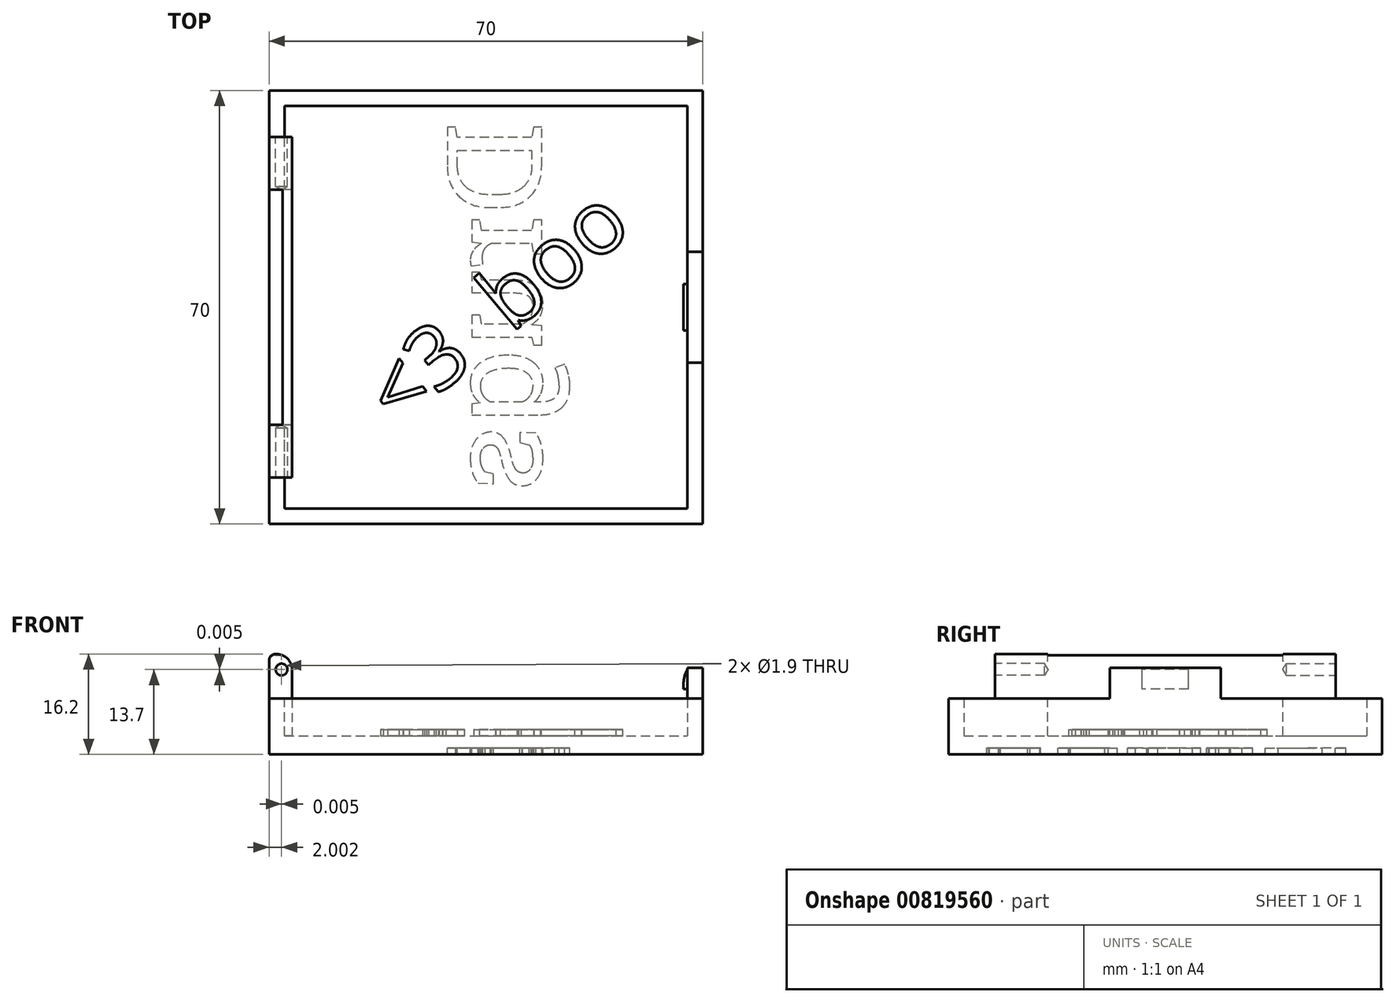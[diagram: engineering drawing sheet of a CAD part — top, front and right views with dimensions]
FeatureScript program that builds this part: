
annotation { "Feature Type Name" : "Feature", "Feature Type Description" : "" }
export const myFeature = defineFeature(function(context is Context, id is Id, definition is map)
    precondition{}
    {
        {
            var Q0;
            Q0=qCreatedBy(makeId("Top.planeOp"),FACE);
            var sketch = newSketch(context, id + "F0", { "sketchPlane" : qUnion([Q0])});
            skLineSegment(sketch, "E0.bottom", {"start": v(-37.36, -39.62) * mm, "end": v(27.64, -39.62) * mm});
            skLineSegment(sketch, "E0.top", {"start": v(-37.36, 25.38) * mm, "end": v(27.64, 25.38) * mm});
            skLineSegment(sketch, "E0.left", {"start": v(-37.36, -39.62) * mm, "end": v(-37.36, 25.38) * mm});
            skLineSegment(sketch, "E0.right", {"start": v(27.64, -39.62) * mm, "end": v(27.64, 25.38) * mm});
            skLineSegment(sketch, "E1.bottom", {"start": v(-39.86, 27.88) * mm, "end": v(30.14, 27.88) * mm});
            skLineSegment(sketch, "E1.top", {"start": v(-39.86, -42.12) * mm, "end": v(30.14, -42.12) * mm});
            skLineSegment(sketch, "E1.left", {"start": v(-39.86, 27.88) * mm, "end": v(-39.86, -42.12) * mm});
            skLineSegment(sketch, "E1.right", {"start": v(30.14, 27.88) * mm, "end": v(30.14, -42.12) * mm});
            skSolve(sketch);
        }
        {
            var Q0;
            Q0=makeQuery(id+"F0.imprint","IMPRINT",FACE,{"disambiguationData":[TD([[makeQuery(id+"F0.imprint","IMPRINT",EDGE,{"derivedFrom":sQuery(id+"F0.wireOp",EDGE,"E0.bottom")}),-1.0]])]});
            extrude(context, id + "F1", {"entities" : qUnion([Q0]), "depth" : 8 * mm, "offsetDistance" : 25 * mm});
        }
        {
            var Q0;
            Q0=makeQuery(id+"F0.imprint","IMPRINT",FACE,{"disambiguationData":[TD([[makeQuery(id+"F0.imprint","IMPRINT",EDGE,{"derivedFrom":sQuery(id+"F0.wireOp",EDGE,"E0.bottom")}),1.0]])]});
            extrude(context, id + "F2", {"entities" : qUnion([Q0]), "operationType" : NewBodyOperationType.ADD, "depth" : 2 * mm, "offsetDistance" : 25 * mm});
        }
        {
            var Q0;
            Q0=makeQuery(id+"F1.opExtrude","CAP_FACE",FACE,{"disambiguationData":[OSD([sQuery(id+"F0.wireOp",EDGE,"E0.bottom"),sQuery(id+"F0.wireOp",EDGE,"E0.top"),sQuery(id+"F0.wireOp",EDGE,"E0.left"),sQuery(id+"F0.wireOp",EDGE,"E0.right"),sQuery(id+"F0.wireOp",EDGE,"E1.bottom"),sQuery(id+"F0.wireOp",EDGE,"E1.top"),sQuery(id+"F0.wireOp",EDGE,"E1.left"),sQuery(id+"F0.wireOp",EDGE,"E1.right")])],"isStart":false});
            var sketch = newSketch(context, id + "F3", { "sketchPlane" : qUnion([Q0])});
            skLineSegment(sketch, "E2.bottom", {"start": v(30.14, -16.06) * mm, "end": v(27.64, -16.06) * mm});
            skLineSegment(sketch, "E2.top", {"start": v(30.14, 1.82) * mm, "end": v(27.64, 1.82) * mm});
            skLineSegment(sketch, "E2.left", {"start": v(30.14, -16.06) * mm, "end": v(30.14, 1.82) * mm});
            skLineSegment(sketch, "E2.right", {"start": v(27.64, -16.06) * mm, "end": v(27.64, 1.82) * mm});
            skPoint(sketch, "E3", {"position": v(30.14, -7.12) * mm});
            skSolve(sketch);
        }
        {
            var Q0;
            Q0=makeQuery(id+"F3.imprint","IMPRINT",FACE,{"disambiguationData":[TD([[makeQuery(id+"F3.imprint","IMPRINT",EDGE,{"derivedFrom":sQuery(id+"F3.wireOp",EDGE,"E2.bottom")}),-1.0]])]});
            extrude(context, id + "F4", {"entities" : qUnion([Q0]), "operationType" : NewBodyOperationType.ADD, "depth" : 5 * mm, "offsetDistance" : 25 * mm});
        }
        {
            var Q0;
            Q0=makeQuery(id+"F4.boolean.opBoolean","MERGE",FACE,{"derivedFrom":[makeQuery(id+"F1.opExtrude","SWEPT_FACE",FACE,{"disambiguationData":[OSD([sQuery(id+"F0.wireOp",EDGE,"E0.right")])]}),makeQuery(id+"F4.opExtrude","SWEPT_FACE",FACE,{"disambiguationData":[OSD([sQuery(id+"F3.wireOp",EDGE,"E2.right")])]})]});
            var sketch = newSketch(context, id + "F5", { "sketchPlane" : qUnion([Q0])});
            skLineSegment(sketch, "E4.bottom", {"start": v(3.38, 9.55) * mm, "end": v(10.86, 9.55) * mm});
            skLineSegment(sketch, "E4.top", {"start": v(3.38, 12.75) * mm, "end": v(10.86, 12.75) * mm});
            skLineSegment(sketch, "E4.left", {"start": v(3.38, 9.55) * mm, "end": v(3.38, 12.75) * mm});
            skLineSegment(sketch, "E4.right", {"start": v(10.86, 9.55) * mm, "end": v(10.86, 12.75) * mm});
            skSolve(sketch);
        }
        {
            var Q0;
            Q0=makeQuery(id+"F5.imprint","IMPRINT",FACE,{"disambiguationData":[TD([[makeQuery(id+"F5.imprint","IMPRINT",EDGE,{"derivedFrom":sQuery(id+"F5.wireOp",EDGE,"E4.bottom")}),1.0]])]});
            extrude(context, id + "F6", {"entities" : qUnion([Q0]), "operationType" : NewBodyOperationType.ADD, "depth" : .6 * mm, "offsetDistance" : 25 * mm});
        }
        {
            var Q0;
            Q0=makeQuery(id+"F6.opExtrude","CAP_EDGE",EDGE,{"disambiguationData":[OSD([sQuery(id+"F5.wireOp",EDGE,"E4.top")])],"isStart":false});
            fillet(context, id + "F7", {"entities" : qUnion([Q0]), "radius" : 5 * mm, "tangentPropagation" : true, "allowEdgeOverflow" : false});
        }
        {
            var Q0;
            Q0=makeQuery(id+"F1.opExtrude","CAP_FACE",FACE,{"disambiguationData":[OSD([sQuery(id+"F0.wireOp",EDGE,"E0.bottom"),sQuery(id+"F0.wireOp",EDGE,"E0.top"),sQuery(id+"F0.wireOp",EDGE,"E0.left"),sQuery(id+"F0.wireOp",EDGE,"E0.right"),sQuery(id+"F0.wireOp",EDGE,"E1.bottom"),sQuery(id+"F0.wireOp",EDGE,"E1.top"),sQuery(id+"F0.wireOp",EDGE,"E1.left"),sQuery(id+"F0.wireOp",EDGE,"E1.right")])],"isStart":false});
            var sketch = newSketch(context, id + "F8", { "sketchPlane" : qUnion([Q0])});
            skLineSegment(sketch, "E5.bottom", {"start": v(-39.86, 11.88) * mm, "end": v(-36.16, 11.88) * mm});
            skLineSegment(sketch, "E5.top", {"start": v(-39.86, -26.12) * mm, "end": v(-36.16, -26.12) * mm});
            skLineSegment(sketch, "E5.left", {"start": v(-39.86, 11.88) * mm, "end": v(-39.86, -26.12) * mm});
            skLineSegment(sketch, "E5.right", {"start": v(-36.16, 11.88) * mm, "end": v(-36.16, -26.12) * mm});
            skSolve(sketch);
        }
        {
            var Q0;
            {var subQ0=sQuery(id+"F8.wireOp",EDGE,"E5.right");Q0=makeQuery(id+"F8.imprint","IMPRINT",FACE,{"disambiguationData":[TD([[makeQuery(id+"F8.imprint","IMPRINT",EDGE,{"derivedFrom":subQ0}),-1.0]])]});}
            var Q1;
            {var subQ0=sQuery(id+"F8.wireOp",EDGE,"E5.left");Q1=makeQuery(id+"F8.imprint","IMPRINT",FACE,{"disambiguationData":[TD([[makeQuery(id+"F8.imprint","IMPRINT",EDGE,{"derivedFrom":subQ0}),1.0]])]});}
            extrude(context, id + "F9", {"entities" : qUnion([Q0, Q1]), "operationType" : NewBodyOperationType.ADD, "depth" : 7 * mm, "offsetDistance" : 25 * mm});
        }
        {
            var Q0;
            {var subQ0=sQuery(id+"F8.wireOp",EDGE,"E5.right");Q0=makeQuery(id+"F8.imprint","IMPRINT",FACE,{"disambiguationData":[TD([[makeQuery(id+"F8.imprint","IMPRINT",EDGE,{"derivedFrom":subQ0}),-1.0]])]});}
            extrude(context, id + "F10", {"entities" : qUnion([Q0]), "operationType" : NewBodyOperationType.ADD, "endBound" : BoundingType.UP_TO_NEXT, "oppositeDirection" : true, "depth" : 5 * mm, "offsetDistance" : 25 * mm});
        }
        {
            var Q0;
            {var subQ0=sQuery(id+"F0.wireOp",EDGE,"E0.top");var subQ1=sQuery(id+"F0.wireOp",EDGE,"E1.right");var subQ2=sQuery(id+"F0.wireOp",EDGE,"E1.left");var subQ3=sQuery(id+"F0.wireOp",EDGE,"E0.left");var subQ5=sQuery(id+"F0.wireOp",EDGE,"E0.right");var subQ6=sQuery(id+"F0.wireOp",EDGE,"E1.bottom");Q0=makeQuery(id+"F9.boolean.opBoolean","SPLIT",FACE,{"disambiguationData":[TD([makeQuery(id+"F1.opExtrude","SWEPT_FACE",FACE,{"disambiguationData":[OSD([subQ0])]})])],"derivedFrom":makeQuery(id+"F1.opExtrude","CAP_FACE",FACE,{"disambiguationData":[OSD([sQuery(id+"F0.wireOp",EDGE,"E0.bottom"),subQ0,subQ3,subQ5,subQ6,sQuery(id+"F0.wireOp",EDGE,"E1.top"),subQ2,subQ1])],"isStart":false})});}
            var sketch = newSketch(context, id + "F11", { "sketchPlane" : qUnion([Q0])});
            skLineSegment(sketch, "E6.bottom", {"start": v(-39.86, 20.38) * mm, "end": v(-36.16, 20.38) * mm});
            skLineSegment(sketch, "E6.top", {"start": v(-39.86, 11.88) * mm, "end": v(-36.16, 11.88) * mm});
            skLineSegment(sketch, "E6.left", {"start": v(-39.86, 20.38) * mm, "end": v(-39.86, 11.88) * mm});
            skLineSegment(sketch, "E6.right", {"start": v(-36.16, 20.38) * mm, "end": v(-36.16, 11.88) * mm});
            skLineSegment(sketch, "E7.bottom", {"start": v(-39.85, -26.11) * mm, "end": v(-36.15, -26.11) * mm});
            skLineSegment(sketch, "E7.top", {"start": v(-39.85, -34.61) * mm, "end": v(-36.15, -34.61) * mm});
            skLineSegment(sketch, "E7.left", {"start": v(-39.85, -26.11) * mm, "end": v(-39.85, -34.61) * mm});
            skLineSegment(sketch, "E7.right", {"start": v(-36.15, -26.11) * mm, "end": v(-36.15, -34.61) * mm});
            skSolve(sketch);
        }
        {
            var Q0;
            Q0=qSketchRegion(id+"F11",true);
            extrude(context, id + "F12", {"entities" : qUnion([Q0]), "operationType" : NewBodyOperationType.ADD, "depth" : 7.2 * mm, "offsetDistance" : 25 * mm});
        }
        {
            var Q0;
            Q0=makeQuery(id+"F12.opExtrude","SWEPT_FACE",FACE,{"disambiguationData":[OSD([sQuery(id+"F11.wireOp",EDGE,"E6.bottom")])]});
            var sketch = newSketch(context, id + "F13", { "sketchPlane" : qUnion([Q0])});
            skPoint(sketch, "E8", {"position": v(37.86, 12.7) * mm});
            skPoint(sketch, "E9", {"position": v(14.71, -29.21) * mm});
            skPoint(sketch, "E10", {"position": v(38, 15.2) * mm});
            skSolve(sketch);
        }
        {
            var Q0;
            Q0=sQuery(id+"F13.wireOp",VERTEX,"E8");
            var Q1;
            Q1=makeQuery(id+"F1.opExtrude","SWEPT_BODY",BODY,{"disambiguationData":[OSD([sQuery(id+"F0.wireOp",EDGE,"E0.bottom"),sQuery(id+"F0.wireOp",EDGE,"E0.top"),sQuery(id+"F0.wireOp",EDGE,"E0.left"),sQuery(id+"F0.wireOp",EDGE,"E0.right"),sQuery(id+"F0.wireOp",EDGE,"E1.bottom"),sQuery(id+"F0.wireOp",EDGE,"E1.top"),sQuery(id+"F0.wireOp",EDGE,"E1.left"),sQuery(id+"F0.wireOp",EDGE,"E1.right")])]});
            hole(context, id + "F14", {"style" : HoleStyle.SIMPLE, "endStyle" : HoleEndStyle.BLIND, "holeDiameter" : 1.9 * mm, "majorDiameter" : 5 * mm, "holeDepth" : 8 * mm, "isTappedThrough" : true, "tappedDepth" : 12 * mm, "tapClearance" : 3, "locations" : qUnion([Q0]), "scope" : qUnion([Q1])});
        }
        {
            var Q0;
            Q0=makeQuery(id+"F12.opExtrude","SWEPT_FACE",FACE,{"disambiguationData":[OSD([sQuery(id+"F11.wireOp",EDGE,"E7.top")])]});
            var sketch = newSketch(context, id + "F15", { "sketchPlane" : qUnion([Q0])});
            skPoint(sketch, "E11", {"position": v(-37.85, 12.7) * mm});
            skPoint(sketch, "E12", {"position": v(-38, 15.2) * mm});
            skSolve(sketch);
        }
        {
            var Q0;
            Q0=sQuery(id+"F15.wireOp",VERTEX,"E11");
            var Q1;
            Q1=makeQuery(id+"F1.opExtrude","SWEPT_BODY",BODY,{"disambiguationData":[OSD([sQuery(id+"F0.wireOp",EDGE,"E0.bottom"),sQuery(id+"F0.wireOp",EDGE,"E0.top"),sQuery(id+"F0.wireOp",EDGE,"E0.left"),sQuery(id+"F0.wireOp",EDGE,"E0.right"),sQuery(id+"F0.wireOp",EDGE,"E1.bottom"),sQuery(id+"F0.wireOp",EDGE,"E1.top"),sQuery(id+"F0.wireOp",EDGE,"E1.left"),sQuery(id+"F0.wireOp",EDGE,"E1.right")])]});
            hole(context, id + "F16", {"style" : HoleStyle.SIMPLE, "endStyle" : HoleEndStyle.BLIND, "holeDiameter" : 1.9 * mm, "majorDiameter" : 5 * mm, "holeDepth" : 8 * mm, "isTappedThrough" : true, "tappedDepth" : 12 * mm, "tapClearance" : 3, "locations" : qUnion([Q0]), "scope" : qUnion([Q1])});
        }
        {
            var Q0;
            {var subQ0=sQuery(id+"F0.wireOp",EDGE,"E0.right");var subQ1=sQuery(id+"F0.wireOp",EDGE,"E0.left");var subQ2=sQuery(id+"F0.wireOp",EDGE,"E0.top");var subQ3=sQuery(id+"F0.wireOp",EDGE,"E0.bottom");Q0=makeQuery(id+"F2.boolean.opBoolean","MERGE",FACE,{"derivedFrom":[makeQuery(id+"F1.opExtrude","CAP_FACE",FACE,{"disambiguationData":[OSD([subQ3,subQ2,subQ1,subQ0,sQuery(id+"F0.wireOp",EDGE,"E1.bottom"),sQuery(id+"F0.wireOp",EDGE,"E1.top"),sQuery(id+"F0.wireOp",EDGE,"E1.left"),sQuery(id+"F0.wireOp",EDGE,"E1.right")])],"isStart":true}),makeQuery(id+"F2.opExtrude","CAP_FACE",FACE,{"disambiguationData":[OSD([subQ3,subQ2,subQ1,subQ0])],"isStart":true})]});}
            var sketch = newSketch(context, id + "F17", { "sketchPlane" : qUnion([Q0])});
            skText(sketch, "E13", { "text": "Drugs", "fontName": "RobotoSlab-Regular.ttf"});
            const initialGuessF17  = {"E13": [0.00413, -0.02273, 0, 1, 0.0154]};
            skSetInitialGuess(sketch, initialGuessF17);
            skSolve(sketch);
        }
        {
            var Q0;
            Q0=makeQuery(id+"F17.imprint","IMPRINT",FACE,{"disambiguationData":[TD([[makeQuery(id+"F17.imprint","IMPRINT",EDGE,{"derivedFrom":sQuery(id+"F17.wireOp",EDGE,"E13.sketch_text.stroke-0")}),1.0]])]});
            var Q1;
            Q1=makeQuery(id+"F17.imprint","IMPRINT",FACE,{"disambiguationData":[TD([[makeQuery(id+"F17.imprint","IMPRINT",EDGE,{"derivedFrom":sQuery(id+"F17.wireOp",EDGE,"E13.sketch_text.stroke-86")}),1.0]])]});
            var Q2;
            Q2=makeQuery(id+"F17.imprint","IMPRINT",FACE,{"disambiguationData":[TD([[makeQuery(id+"F17.imprint","IMPRINT",EDGE,{"derivedFrom":sQuery(id+"F17.wireOp",EDGE,"E13.sketch_text.stroke-13")}),1.0]])]});
            var Q3;
            {var subQ0=sQuery(id+"F0.wireOp",EDGE,"E0.top");var subQ1=sQuery(id+"F0.wireOp",EDGE,"E1.right");var subQ2=sQuery(id+"F0.wireOp",EDGE,"E1.left");var subQ3=sQuery(id+"F0.wireOp",EDGE,"E0.left");var subQ5=sQuery(id+"F0.wireOp",EDGE,"E0.right");var subQ6=sQuery(id+"F0.wireOp",EDGE,"E1.bottom");Q3=makeQuery(id+"F9.boolean.opBoolean","SPLIT",FACE,{"disambiguationData":[TD([makeQuery(id+"F1.opExtrude","SWEPT_FACE",FACE,{"disambiguationData":[OSD([subQ0])]})])],"derivedFrom":makeQuery(id+"F1.opExtrude","CAP_FACE",FACE,{"disambiguationData":[OSD([sQuery(id+"F0.wireOp",EDGE,"E0.bottom"),subQ0,subQ3,subQ5,subQ6,sQuery(id+"F0.wireOp",EDGE,"E1.top"),subQ2,subQ1])],"isStart":false})});}
            var Q4;
            Q4=qConstructionFilter(qBodyType(qCreatedBy(id+"F17",EDGE),BodyType.WIRE),ConstructionObject.NO);
            extrude(context, id + "F18", {"entities" : qUnion([Q0, Q1, Q2, Q3]), "operationType" : NewBodyOperationType.ADD, "surfaceOperationType" : NewSurfaceOperationType.ADD, "surfaceEntities" : qUnion([Q4]), "depth" : 1 * mm, "offsetDistance" : 25 * mm});
        }
        {
            var Q0;
            Q0=makeQuery(id+"F2.opExtrude","CAP_FACE",FACE,{"disambiguationData":[OSD([sQuery(id+"F0.wireOp",EDGE,"E0.bottom"),sQuery(id+"F0.wireOp",EDGE,"E0.top"),sQuery(id+"F0.wireOp",EDGE,"E0.left"),sQuery(id+"F0.wireOp",EDGE,"E0.right")])],"isStart":false});
            var sketch = newSketch(context, id + "F19", { "sketchPlane" : qUnion([Q0])});
            skText(sketch, "E14", { "text": "<3  boo", "fontName": "OpenSans-Regular.ttf"});
            skLineSegment(sketch, "E15.0", {"start": v(-19.03, -26.77) * mm, "end": v(19.28, 5.37) * mm, "construction": true});
            skLineSegment(sketch, "E15.1", {"start": v(-19.03, -26.77) * mm, "end": v(-19.03, -26.77) * mm});
            const initialGuessF19  = {"E14": [-0.01903, -0.02677, 0.76604, 0.64279, 0.0103]};
            skSetInitialGuess(sketch, initialGuessF19);
            skSolve(sketch);
        }
        {
            var Q0;
            Q0=qSketchRegion(id+"F19",true);
            extrude(context, id + "F20", {"entities" : qUnion([Q0]), "operationType" : NewBodyOperationType.ADD, "depth" : 1 * mm, "offsetDistance" : 25 * mm});
        }
        {
            var Q0;
            Q0=makeQuery(id+"F12.opExtrude","CAP_EDGE",EDGE,{"disambiguationData":[OSD([sQuery(id+"F11.wireOp",EDGE,"E7.right")])],"isStart":false});
            fillet(context, id + "F21", {"entities" : qUnion([Q0]), "radius" : 2.5 * mm, "tangentPropagation" : true, "allowEdgeOverflow" : false});
        }
        {
            var Q0;
            Q0=makeQuery(id+"F9.opExtrude","CAP_EDGE",EDGE,{"disambiguationData":[OSD([sQuery(id+"F8.wireOp",EDGE,"E5.left")])],"isStart":false});
            fillet(context, id + "F22", {"entities" : qUnion([Q0]), "radius" : 1 * mm, "tangentPropagation" : true, "allowEdgeOverflow" : false});
        }
        {
            var Q0;
            Q0=makeQuery(id+"F12.opExtrude","CAP_EDGE",EDGE,{"disambiguationData":[OSD([sQuery(id+"F11.wireOp",EDGE,"E7.left")])],"isStart":false});
            var Q1;
            Q1=makeQuery(id+"F12.opExtrude","CAP_EDGE",EDGE,{"disambiguationData":[OSD([sQuery(id+"F11.wireOp",EDGE,"E6.left")])],"isStart":false});
            fillet(context, id + "F23", {"entities" : qUnion([Q0, Q1]), "radius" : 1 * mm, "tangentPropagation" : true, "allowEdgeOverflow" : false});
        }
    });
